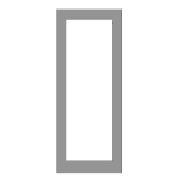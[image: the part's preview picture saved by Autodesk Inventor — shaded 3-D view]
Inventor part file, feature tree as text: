
AUTODESK INVENTOR PART (.ipt)
format: ipt  version: 2020 (Build 240168000, 168)  size: 125,952 bytes
history: native  units: in
note: dims shown in document units (in); Inventor stores cm internally (conversion verified against a paired STEP export)
features: other x4, plane x3, sketch x3, split x2
ambient origin geometry x8: Origin, YZ Plane, XZ Plane, XY Plane, X Axis, Y Axis, Z Axis, Center Point
bodies: Solid1 (feature_tree), Body (feature_tree)
feature tree (12):
  other  "Driven Length"
  other  "Frame Generator"
  other  "Start Plane"
  other  "End Plane"
  plane  "Work Plane6"
  split  "Split1"
  plane  "Work Plane7"
  split  "Split2"
  sketch  "Sketch"  dims[d2=0.125in d3=0.125in d6=0.5in d7=23.5in d8=0.13in d9=0.0in d14=90.0deg d11=23.0in]
  sketch  "Sketch6"  dims[d0=1.0in]
  plane  "Work Plane5"
  sketch  "Sketch7"  dims[d1=3.0in]
